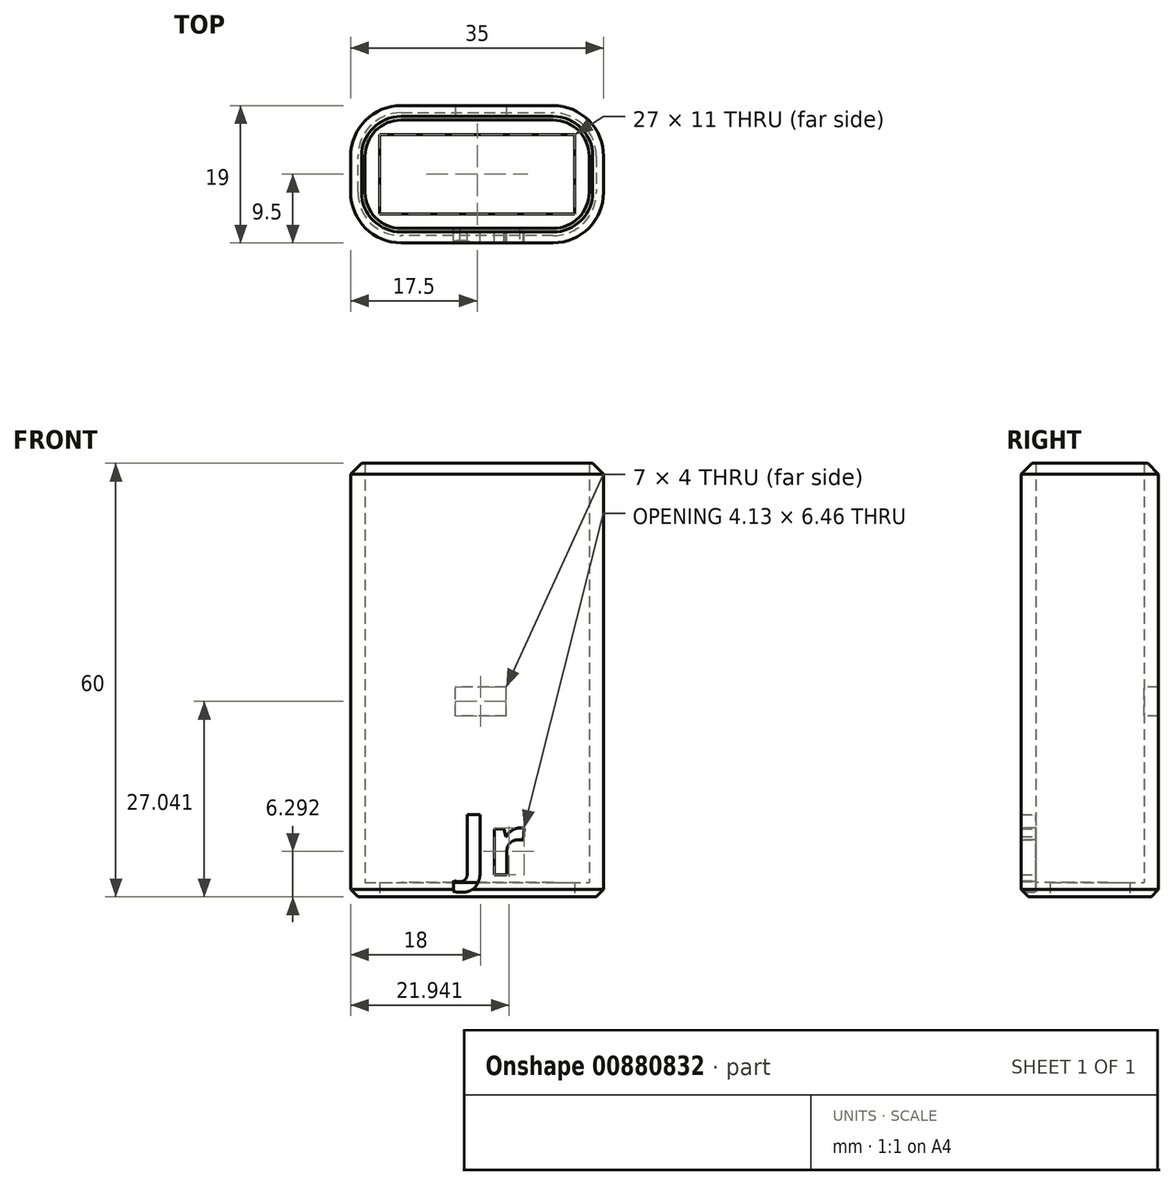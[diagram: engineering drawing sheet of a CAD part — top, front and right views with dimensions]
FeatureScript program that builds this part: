
annotation { "Feature Type Name" : "Feature", "Feature Type Description" : "" }
export const myFeature = defineFeature(function(context is Context, id is Id, definition is map)
    precondition{}
    {
        {
            var Q0;
            Q0=qCreatedBy(makeId("Top.planeOp"),FACE);
            var sketch = newSketch(context, id + "F0", { "sketchPlane" : qUnion([Q0])});
            skLineSegment(sketch, "E0.bottom", {"start": v(5, 0) * mm, "end": v(26, 0) * mm});
            skLineSegment(sketch, "E0.top", {"start": v(5, 15) * mm, "end": v(26, 15) * mm});
            skLineSegment(sketch, "E0.left", {"start": v(0, 5) * mm, "end": v(0, 10) * mm});
            skLineSegment(sketch, "E0.right", {"start": v(31, 5) * mm, "end": v(31, 10) * mm});
            skPoint(sketch, "E1.visualSharp", {"position": v(0, 15) * mm});
            skArc(sketch, "E1.filletArc", {"start": v(5, 15) * mm, "mid": v(1.46, 13.54) * mm, "end": v(0, 10) * mm});
            skPoint(sketch, "E2.visualSharp", {"position": v(0, 0) * mm});
            skArc(sketch, "E2.filletArc", {"start": v(0, 5) * mm, "mid": v(1.46, 1.46) * mm, "end": v(5, 0) * mm});
            skPoint(sketch, "E3.visualSharp", {"position": v(31, 15) * mm});
            skArc(sketch, "E3.filletArc", {"start": v(31, 10) * mm, "mid": v(29.54, 13.54) * mm, "end": v(26, 15) * mm});
            skPoint(sketch, "E4.visualSharp", {"position": v(31, 0) * mm});
            skArc(sketch, "E4.filletArc", {"start": v(26, 0) * mm, "mid": v(29.54, 1.46) * mm, "end": v(31, 5) * mm});
            skArc(sketch, "E5.0", {"start": v(5, 17) * mm, "mid": v(0.05, 14.95) * mm, "end": v(-2, 10) * mm});
            skLineSegment(sketch, "E5.1", {"start": v(-2, 5) * mm, "end": v(-2, 10) * mm});
            skLineSegment(sketch, "E5.2", {"start": v(5, 17) * mm, "end": v(26, 17) * mm});
            skArc(sketch, "E5.3", {"start": v(-2, 5) * mm, "mid": v(0.05, 0.05) * mm, "end": v(5, -2) * mm});
            skArc(sketch, "E5.4", {"start": v(33, 10) * mm, "mid": v(30.95, 14.95) * mm, "end": v(26, 17) * mm});
            skLineSegment(sketch, "E5.5", {"start": v(33, 5) * mm, "end": v(33, 10) * mm});
            skArc(sketch, "E5.6", {"start": v(26, -2) * mm, "mid": v(30.95, 0.05) * mm, "end": v(33, 5) * mm});
            skLineSegment(sketch, "E5.7", {"start": v(5, -2) * mm, "end": v(26, -2) * mm});
            skLineSegment(sketch, "E6.0", {"start": v(2, 13) * mm, "end": v(29, 13) * mm});
            skLineSegment(sketch, "E6.1", {"start": v(2, 2) * mm, "end": v(2, 13) * mm});
            skLineSegment(sketch, "E6.2", {"start": v(2, 2) * mm, "end": v(29, 2) * mm});
            skLineSegment(sketch, "E6.3", {"start": v(29, 2) * mm, "end": v(29, 13) * mm});
            skSolve(sketch);
        }
        {
            var Q0;
            Q0=makeQuery(id+"F0.imprint","IMPRINT",FACE,{"disambiguationData":[TD([[makeQuery(id+"F0.imprint","IMPRINT",EDGE,{"derivedFrom":sQuery(id+"F0.wireOp",EDGE,"E0.bottom")}),1.0]])]});
            var Q1;
            Q1=makeQuery(id+"F0.imprint","IMPRINT",FACE,{"disambiguationData":[TD([[makeQuery(id+"F0.imprint","IMPRINT",EDGE,{"derivedFrom":sQuery(id+"F0.wireOp",EDGE,"E0.bottom")}),-1.0]])]});
            extrude(context, id + "F1", {"entities" : qUnion([Q0, Q1]), "depth" : 2 * mm, "offsetDistance" : 25 * mm});
        }
        {
            var Q0;
            Q0=makeQuery(id+"F0.imprint","IMPRINT",FACE,{"disambiguationData":[TD([[makeQuery(id+"F0.imprint","IMPRINT",EDGE,{"derivedFrom":sQuery(id+"F0.wireOp",EDGE,"E0.bottom")}),-1.0]])]});
            extrude(context, id + "F2", {"entities" : qUnion([Q0]), "operationType" : NewBodyOperationType.ADD, "depth" : 60 * mm, "offsetDistance" : 25 * mm});
        }
        {
            var Q0;
            Q0=qCreatedBy(makeId("Front.planeOp"),FACE);
            var sketch = newSketch(context, id + "F3", { "sketchPlane" : qUnion([Q0])});
            skLineSegment(sketch, "E7.bottom", {"start": v(12.5, 29.04) * mm, "end": v(19.5, 29.04) * mm});
            skLineSegment(sketch, "E7.top", {"start": v(12.5, 25.04) * mm, "end": v(19.5, 25.04) * mm});
            skLineSegment(sketch, "E7.left", {"start": v(12.5, 29.04) * mm, "end": v(12.5, 25.04) * mm});
            skLineSegment(sketch, "E7.right", {"start": v(19.5, 29.04) * mm, "end": v(19.5, 25.04) * mm});
            skSolve(sketch);
        }
        {
            var Q0;
            Q0=makeQuery(id+"F3.imprint","IMPRINT",FACE,{"disambiguationData":[TD([[makeQuery(id+"F3.imprint","IMPRINT",EDGE,{"derivedFrom":sQuery(id+"F3.wireOp",EDGE,"E7.bottom")}),-1.0]])]});
            extrude(context, id + "F4", {"entities" : qUnion([Q0]), "operationType" : NewBodyOperationType.REMOVE, "oppositeDirection" : true, "depth" : 25 * mm, "offsetDistance" : 25 * mm});
        }
        {
            var Q0;
            Q0=qCreatedBy(makeId("Front.planeOp"),FACE);
            var sketch = newSketch(context, id + "F5", { "sketchPlane" : qUnion([Q0])});
            skText(sketch, "E8", { "text": "Jr", "fontName": "OpenSans-Bold.ttf"});
            const initialGuessF5  = {"E8": [0.01312, 0.00306, 1, 0, 0.00837]};
            skSetInitialGuess(sketch, initialGuessF5);
            skSolve(sketch);
        }
        {
            var Q0;
            Q0 = qSketchRegion(id + "F5", true);
            extrude(context, id + "F6", {"entities" : qUnion([Q0]), "operationType" : NewBodyOperationType.REMOVE, "depth" : 25 * mm, "offsetDistance" : 25 * mm});
        }
        {
            var Q0;
            Q0=makeQuery(id+"F1.opExtrude","CAP_EDGE",EDGE,{"disambiguationData":[OSD([sQuery(id+"F0.wireOp",EDGE,"E5.7")])],"isStart":true});
            var Q1;
            Q1=makeQuery(id+"F1.opExtrude","CAP_EDGE",EDGE,{"disambiguationData":[OSD([sQuery(id+"F0.wireOp",EDGE,"E5.3")])],"isStart":true});
            var Q2;
            Q2=makeQuery(id+"F1.opExtrude","CAP_EDGE",EDGE,{"disambiguationData":[OSD([sQuery(id+"F0.wireOp",EDGE,"E5.1")])],"isStart":true});
            var Q3;
            Q3=makeQuery(id+"F1.opExtrude","CAP_EDGE",EDGE,{"disambiguationData":[OSD([sQuery(id+"F0.wireOp",EDGE,"E5.0")])],"isStart":true});
            var Q4;
            Q4=makeQuery(id+"F1.opExtrude","CAP_EDGE",EDGE,{"disambiguationData":[OSD([sQuery(id+"F0.wireOp",EDGE,"E5.2")])],"isStart":true});
            var Q5;
            Q5=makeQuery(id+"F1.opExtrude","CAP_EDGE",EDGE,{"disambiguationData":[OSD([sQuery(id+"F0.wireOp",EDGE,"E5.4")])],"isStart":true});
            var Q6;
            Q6=makeQuery(id+"F1.opExtrude","CAP_EDGE",EDGE,{"disambiguationData":[OSD([sQuery(id+"F0.wireOp",EDGE,"E5.5")])],"isStart":true});
            var Q7;
            Q7=makeQuery(id+"F1.opExtrude","CAP_EDGE",EDGE,{"disambiguationData":[OSD([sQuery(id+"F0.wireOp",EDGE,"E5.6")])],"isStart":true});
            chamfer(context, id + "F7", {"entities" : qUnion([Q0, Q1, Q2, Q3, Q4, Q5, Q6, Q7]), "width" : 1 * mm, "tangentPropagation" : true});
        }
        {
            var Q0;
            Q0=makeQuery(id+"F2.opExtrude","CAP_EDGE",EDGE,{"disambiguationData":[OSD([sQuery(id+"F0.wireOp",EDGE,"E5.7")])],"isStart":false});
            var Q1;
            Q1=makeQuery(id+"F2.opExtrude","CAP_EDGE",EDGE,{"disambiguationData":[OSD([sQuery(id+"F0.wireOp",EDGE,"E5.6")])],"isStart":false});
            var Q2;
            Q2=makeQuery(id+"F2.opExtrude","CAP_EDGE",EDGE,{"disambiguationData":[OSD([sQuery(id+"F0.wireOp",EDGE,"E5.5")])],"isStart":false});
            var Q3;
            Q3=makeQuery(id+"F2.opExtrude","CAP_EDGE",EDGE,{"disambiguationData":[OSD([sQuery(id+"F0.wireOp",EDGE,"E5.4")])],"isStart":false});
            var Q4;
            Q4=makeQuery(id+"F2.opExtrude","CAP_EDGE",EDGE,{"disambiguationData":[OSD([sQuery(id+"F0.wireOp",EDGE,"E5.2")])],"isStart":false});
            var Q5;
            Q5=makeQuery(id+"F2.opExtrude","CAP_EDGE",EDGE,{"disambiguationData":[OSD([sQuery(id+"F0.wireOp",EDGE,"E5.0")])],"isStart":false});
            var Q6;
            Q6=makeQuery(id+"F2.opExtrude","CAP_EDGE",EDGE,{"disambiguationData":[OSD([sQuery(id+"F0.wireOp",EDGE,"E5.1")])],"isStart":false});
            var Q7;
            Q7=makeQuery(id+"F2.opExtrude","CAP_EDGE",EDGE,{"disambiguationData":[OSD([sQuery(id+"F0.wireOp",EDGE,"E5.3")])],"isStart":false});
            chamfer(context, id + "F8", {"entities" : qUnion([Q0, Q1, Q2, Q3, Q4, Q5, Q6, Q7]), "width" : 1.5 * mm, "tangentPropagation" : true});
        }
    });
